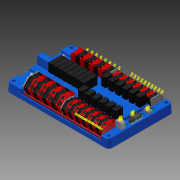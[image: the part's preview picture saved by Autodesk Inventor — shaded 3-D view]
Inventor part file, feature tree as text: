
AUTODESK INVENTOR PART (.ipt)
format: ipt  version: 2013 (Build 170138000, 138)  size: 17,241,600 bytes
history: native  units: in
note: dims shown in document units (in); Inventor stores cm internally (conversion verified against a paired STEP export)
features: other x181, sketch x22, plane x21, pattern_linear x3
ambient origin geometry x8: Origin, YZ Plane, XZ Plane, XY Plane, X Axis, Y Axis, Z Axis, Center Point
bodies: Solid1 (feature_tree)
feature tree (227):
  other  "PD Rev3 Assembly.iam"
  other  "PD Rev3 Bottom.ipt:1"
  other  "CTF040V8.iam:1::CTF040V8_1.ipt:1"
  other  "CTF040V8.iam:1::CTF040V8_2.ipt:1"
  other  "CTF040V8.iam:1::CTF040V8_3.ipt:1"
  other  "PD Rev3 PCB.iam:1::PD Rev3 Board.ipt:1"
  other  "PD Rev3 PCB.iam:1::Wago 745-831 (32A) Block.iam:1::Wago 745-831 (32A):1"
  other  "PD Rev3 PCB.iam:1::Wago 745-831 (32A) Block.iam:1::Wago 745-831 (32A):2"
  other  "PD Rev3 PCB.iam:1::Wago 745-831 (32A) Block.iam:1::Wago 745-831 (32A):3"
  other  "PD Rev3 PCB.iam:1::Wago 745-831 (32A) Block.iam:1::Wago 745-831 (32A):4"
  other  "PD Rev3 PCB.iam:1::Wago 745-831 (32A) Block.iam:1::Wago 745-831 (32A):5"
  other  "PD Rev3 PCB.iam:1::Wago 745-831 (32A) Block.iam:1::Wago 745-831 (32A):6"
  other  "PD Rev3 PCB.iam:1::Wago 745-831 (32A) Block.iam:1::Wago 745-831 (32A):7"
  other  "PD Rev3 PCB.iam:1::Wago 745-831 (32A) Block.iam:1::Wago 745-831 (32A):8"
  other  "PD Rev3 PCB.iam:1::Wago 745-831 (32A) Block.iam:1::Wago 745-831 (32A):9"
  other  "PD Rev3 PCB.iam:1::Wago 745-831 (32A) Block.iam:1::Wago 745-831 (32A):10"
  other  "PD Rev3 PCB.iam:1::Wago 745-831 (32A) Block.iam:1::Wago 745-831 (32A):11"
  other  "PD Rev3 PCB.iam:1::Wago 745-831 (32A) Block.iam:1::Wago 745-831 (32A):12"
  other  "PD Rev3 PCB.iam:1::Wago 745-831 (32A) Block.iam:1::745-300:1"
  other  "PD Rev3 PCB.iam:1::Wago 745-831 (32A) Block.iam:2::Wago 745-831 (32A):1"
  other  "PD Rev3 PCB.iam:1::Wago 745-831 (32A) Block.iam:2::Wago 745-831 (32A):2"
  other  "PD Rev3 PCB.iam:1::Wago 745-831 (32A) Block.iam:2::Wago 745-831 (32A):3"
  other  "PD Rev3 PCB.iam:1::Wago 745-831 (32A) Block.iam:2::Wago 745-831 (32A):4"
  other  "PD Rev3 PCB.iam:1::Wago 745-831 (32A) Block.iam:2::Wago 745-831 (32A):5"
  other  "PD Rev3 PCB.iam:1::Wago 745-831 (32A) Block.iam:2::Wago 745-831 (32A):6"
  other  "PD Rev3 PCB.iam:1::Wago 745-831 (32A) Block.iam:2::Wago 745-831 (32A):7"
  other  "PD Rev3 PCB.iam:1::Wago 745-831 (32A) Block.iam:2::Wago 745-831 (32A):8"
  other  "PD Rev3 PCB.iam:1::Wago 745-831 (32A) Block.iam:2::Wago 745-831 (32A):9"
  other  "PD Rev3 PCB.iam:1::Wago 745-831 (32A) Block.iam:2::Wago 745-831 (32A):10"
  other  "PD Rev3 PCB.iam:1::Wago 745-831 (32A) Block.iam:2::Wago 745-831 (32A):11"
  other  "PD Rev3 PCB.iam:1::Wago 745-831 (32A) Block.iam:2::Wago 745-831 (32A):12"
  other  "PD Rev3 PCB.iam:1::Wago 745-831 (32A) Block.iam:2::745-300:1"
  other  "PD Rev3 PCB.iam:1::Wago 745-851 (76A) Block.iam:1::Wago 745-851 (76A):2"
  other  "PD Rev3 PCB.iam:1::Wago 745-851 (76A) Block.iam:1::Wago 745-851 (76A):1"
  other  "PD Rev3 PCB.iam:1::Wago 745-851 (76A) Block.iam:1::Wago 745-851 (76A):3"
  other  "PD Rev3 PCB.iam:1::Wago 745-851 (76A) Block.iam:1::Wago 745-851 (76A):4"
  other  "PD Rev3 PCB.iam:1::Wago 745-851 (76A) Block.iam:1::Wago 745-851 (76A):5"
  other  "PD Rev3 PCB.iam:1::Wago 745-851 (76A) Block.iam:1::Wago 745-851 (76A):6"
  other  "PD Rev3 PCB.iam:1::Wago 745-851 (76A) Block.iam:1::Wago 745-851 (76A):7"
  other  "PD Rev3 PCB.iam:1::Wago 745-851 (76A) Block.iam:1::Wago 745-851 (76A):8"
  other  "PD Rev3 PCB.iam:1::Wago 745-851 (76A) Block.iam:1::745-500:1"
  other  "PD Rev3 PCB.iam:1::Wago 745-851 (76A) Block.iam:2::Wago 745-851 (76A):2"
  other  "PD Rev3 PCB.iam:1::Wago 745-851 (76A) Block.iam:2::Wago 745-851 (76A):1"
  other  "PD Rev3 PCB.iam:1::Wago 745-851 (76A) Block.iam:2::Wago 745-851 (76A):3"
  other  "PD Rev3 PCB.iam:1::Wago 745-851 (76A) Block.iam:2::Wago 745-851 (76A):4"
  other  "PD Rev3 PCB.iam:1::Wago 745-851 (76A) Block.iam:2::Wago 745-851 (76A):5"
  other  "PD Rev3 PCB.iam:1::Wago 745-851 (76A) Block.iam:2::Wago 745-851 (76A):6"
  other  "PD Rev3 PCB.iam:1::Wago 745-851 (76A) Block.iam:2::Wago 745-851 (76A):7"
  other  "PD Rev3 PCB.iam:1::Wago 745-851 (76A) Block.iam:2::Wago 745-851 (76A):8"
  other  "PD Rev3 PCB.iam:1::Wago 745-851 (76A) Block.iam:2::745-500:1"
  other  "PD Rev3 PCB.iam:1::LED.ipt:1"
  other  "PD Rev3 PCB.iam:1::LED.ipt:2"
  other  "PD Rev3 PCB.iam:1::734-132:1"
  other  "PD Rev3 PCB.iam:1::LED.ipt:3"
  other  "PD Rev3 PCB.iam:1::Wurth Lug.ipt:1"
  other  "PD Rev3 PCB.iam:1::Wurth Lug.ipt:2"
  other  "PD Rev3 PCB.iam:1::Big CB in Holder.ipt:1"
  other  "PD Rev3 PCB.iam:1::Big CB in Holder.ipt:2"
  other  "PD Rev3 PCB.iam:1::Big CB in Holder.ipt:3"
  other  "PD Rev3 PCB.iam:1::Big CB in Holder.ipt:4"
  other  "PD Rev3 PCB.iam:1::Big CB in Holder.ipt:5"
  other  "PD Rev3 PCB.iam:1::Big CB in Holder.ipt:6"
  other  "PD Rev3 PCB.iam:1::Big CB in Holder.ipt:7"
  other  "PD Rev3 PCB.iam:1::Big CB in Holder.ipt:8"
  other  "PD Rev3 PCB.iam:1::Medium CB in Holder.ipt:2"
  other  "PD Rev3 PCB.iam:1::Medium CB in Holder.ipt:1"
  other  "PD Rev3 PCB.iam:1::Medium CB in Holder.ipt:3"
  other  "PD Rev3 PCB.iam:1::Medium CB in Holder.ipt:4"
  other  "PD Rev3 PCB.iam:1::Medium CB in Holder.ipt:5"
  other  "PD Rev3 PCB.iam:1::Medium CB in Holder.ipt:6"
  other  "PD Rev3 PCB.iam:1::Medium CB in Holder.ipt:7"
  other  "PD Rev3 PCB.iam:1::Medium CB in Holder.ipt:8"
  other  "PD Rev3 PCB.iam:1::Medium CB in Holder.ipt:9"
  other  "PD Rev3 PCB.iam:1::Medium CB in Holder.ipt:10"
  other  "PD Rev3 PCB.iam:1::Medium CB in Holder.ipt:11"
  other  "PD Rev3 PCB.iam:1::Medium CB in Holder.ipt:12"
  other  "PD Rev3 PCB.iam:1::739-302:1"
  other  "PD Rev3 PCB.iam:1::CTM040V8.ipt:1"
  other  "PD Rev3 Top.ipt:1"
  other  "PD Rev3 Assembly.iam_Bodies"
  sketch  "Sketch2"  dims[d0=0.3937in]
  other  "Work Point2"
  other  "Work Point3"
  pattern_linear  "Rectangular Pattern1"  Count1=8 Spacing1=0.2953in
  sketch  "Sketch3"  dims[d1=0.125in]
  sketch  "Sketch4"  dims[d2=0.25in d3=3.1496in d5=0.2953in]
  sketch  "Sketch5"  dims[d6=0.125in]
  sketch  "Sketch6"  dims[d7=0.25in]
  sketch  "Sketch7"  dims[d8=0.125in]
  sketch  "Sketch8"  dims[d9=0.25in]
  sketch  "Sketch9"  dims[d10=0.125in]
  sketch  "Sketch10"  dims[d11=0.25in d12=3.1496in d14=0.2953in]
  sketch  "Sketch11"  dims[d15=0.125in]
  other  "Work Point27"
  other  "Work Point28"
  other  "Work Point29"
  other  "Work Point30"
  sketch  "Sketch12"  dims[d16=0.25in]
  sketch  "Sketch13"  dims[d17=0.125in]
  sketch  "Sketch14"  dims[d18=0.25in]
  sketch  "Sketch15"  dims[d19=0.125in]
  sketch  "Sketch16"  dims[d20=0.25in]
  sketch  "Sketch17"  dims[d21=0.125in]
  sketch  "Sketch18"  dims[d22=0.25in]
  sketch  "Sketch19"  dims[d23=0.125in]
  other  "Work Point39"
  other  "Work Point40"
  pattern_linear  "Rectangular Pattern2"  Count1=8 Spacing1=0.2953in
  other  "Work Point55"
  other  "Work Point56"
  other  "Work Point57"
  other  "Work Point58"
  other  "Work Point59"
  other  "Work Point60"
  sketch  "Sketch20"  dims[d24=0.25in]
  sketch  "Sketch21"  dims[d25=0.125in]
  other  "Work Point63"
  other  "Work Point64"
  other  "Work Point65"
  other  "Work Point66"
  sketch  "Sketch22"  dims[d26=0.25in]
  sketch  "Sketch23"  dims[d27=0.125in d28=3.1496in d30=0.3937in]
  other  "Work Point69"
  other  "Work Point70"
  other  "Work Point71"
  other  "Work Point72"
  other  "Work Point73"
  other  "Work Point74"
  other  "Work Point75"
  pattern_linear  "Rectangular Pattern3"  Count1=8 Spacing1=0.3937in
  plane  "Work Plane1"
  other  "Work Axis1"
  plane  "Work Plane2"
  other  "Work Axis2"
  other  "Work Point4"
  other  "Work Point5"
  other  "Work Point6"
  other  "Work Point7"
  other  "Work Point8"
  other  "Work Point9"
  other  "Work Point10"
  other  "Work Point11"
  other  "Work Point12"
  other  "Work Point13"
  other  "Work Point14"
  other  "Work Point15"
  other  "Work Point16"
  other  "Work Point17"
  plane  "Work Plane3"
  other  "Work Axis3"
  plane  "Work Plane4"
  other  "Work Axis4"
  plane  "Work Plane5"
  other  "Work Axis5"
  plane  "Work Plane6"
  other  "Work Axis6"
  plane  "Work Plane7"
  other  "Work Axis7"
  plane  "Work Plane8"
  other  "Work Axis8"
  other  "Work Point41"
  other  "Work Point42"
  other  "Work Point43"
  other  "Work Point44"
  other  "Work Point45"
  other  "Work Point46"
  other  "Work Point47"
  other  "Work Point48"
  other  "Work Point49"
  other  "Work Point50"
  other  "Work Point51"
  other  "Work Point52"
  other  "Work Point53"
  other  "Work Point54"
  other  "Work Axis9"
  other  "Work Axis10"
  other  "Work Axis11"
  other  "Work Axis12"
  plane  "Work Plane9"
  other  "Work Axis13"
  plane  "Work Plane10"
  other  "Work Axis14"
  plane  "Work Plane11"
  other  "Work Axis15"
  plane  "Work Plane12"
  other  "Work Axis16"
  plane  "Work Plane13"
  other  "Work Axis17"
  plane  "Work Plane14"
  other  "Work Axis18"
  plane  "Work Plane15"
  other  "Work Axis19"
  plane  "Work Plane16"
  other  "Work Axis20"
  plane  "Work Plane17"
  other  "Work Axis21"
  plane  "Work Plane18"
  other  "Work Axis22"
  plane  "Work Plane19"
  other  "Work Axis23"
  plane  "Work Plane20"
  other  "Work Axis24"
  other  "Work Axis25"
  other  "Work Axis26"
  plane  "Work Plane21"
  other  "Work Axis27"
  other  "Work Point76"
  other  "Work Point77"
  other  "Work Point78"
  other  "Work Point79"
  other  "Work Point80"
  other  "Work Point81"
  other  "Work Point82"
  other  "Work Point83"
  other  "Work Point84"
  other  "Work Point85"
  other  "Work Point86"
  other  "Work Point87"
  other  "Work Point88"
  other  "Work Point89"
  other  "Work Point90"
  other  "Work Point91"
  other  "Work Point92"
  other  "Work Point93"
  other  "Work Point94"
  other  "Work Point95"
  other  "Work Point96"
